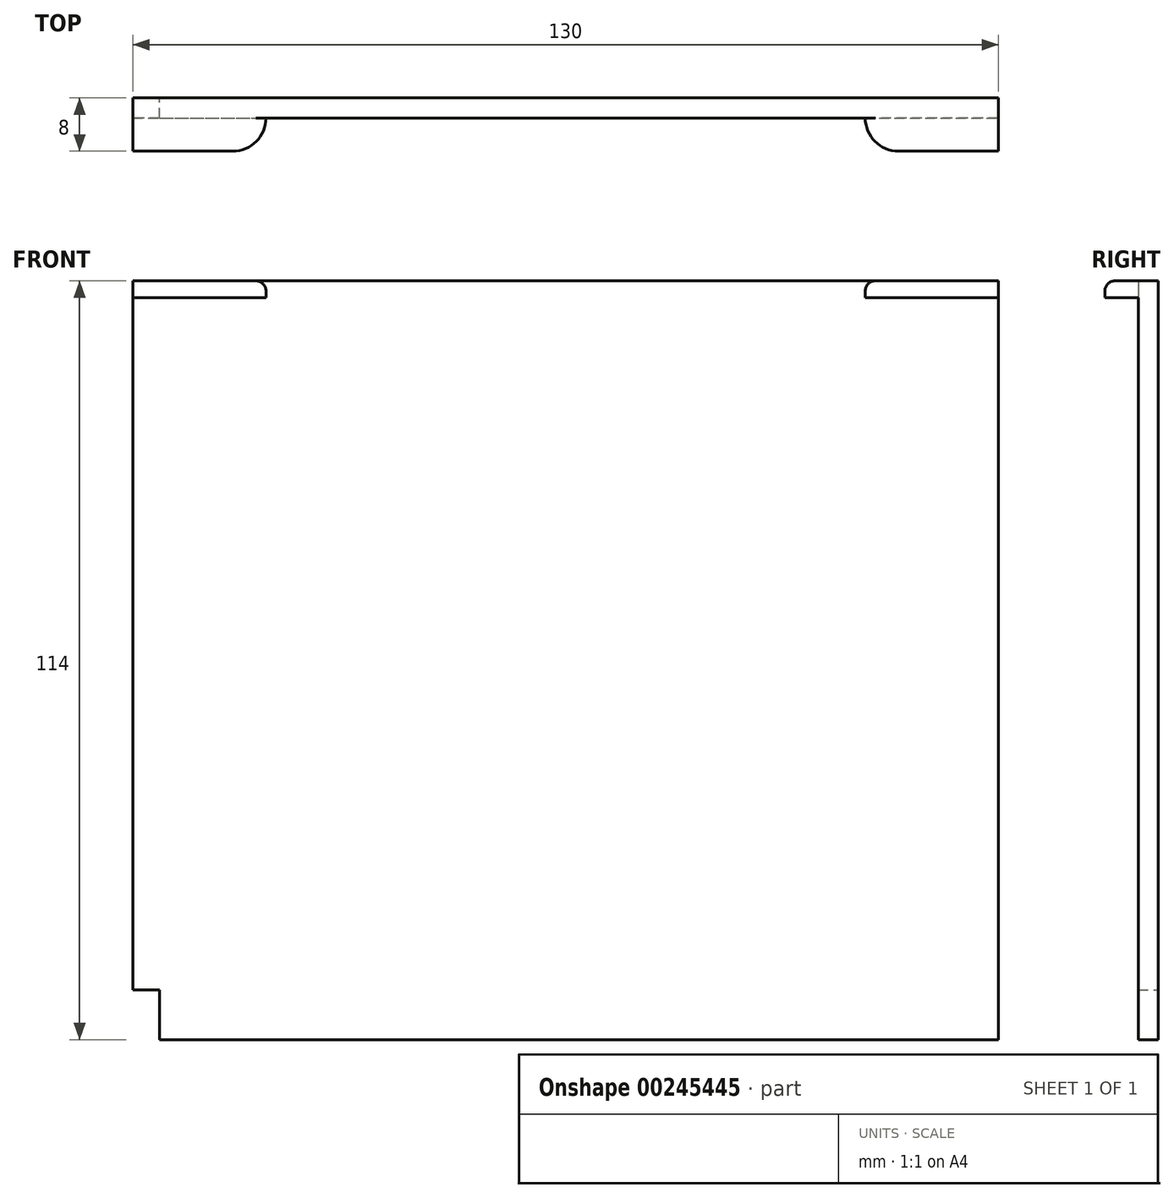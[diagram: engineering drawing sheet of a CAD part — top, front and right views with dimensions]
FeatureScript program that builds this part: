
annotation { "Feature Type Name" : "Feature", "Feature Type Description" : "" }
export const myFeature = defineFeature(function(context is Context, id is Id, definition is map)
    precondition{}
    {
        {
            var Q0;
            Q0=qCreatedBy(makeId("Front.planeOp"),FACE);
            var sketch = newSketch(context, id + "F0", { "sketchPlane" : qUnion([Q0])});
            skLineSegment(sketch, "E0.bottom", {"start": v(0, 0) * mm, "end": v(130, 0) * mm});
            skLineSegment(sketch, "E0.top", {"start": v(0, 114) * mm, "end": v(130, 114) * mm});
            skLineSegment(sketch, "E0.left", {"start": v(0, 0) * mm, "end": v(0, 114) * mm});
            skLineSegment(sketch, "E0.right", {"start": v(130, 0) * mm, "end": v(130, 114) * mm});
            skSolve(sketch);
        }
        {
            var Q0;
            Q0=qSketchRegion(id+"F0",true);
            extrude(context, id + "F1", {"entities" : qUnion([Q0]), "depth" : 3 * mm});
        }
        {
            var Q0;
            Q0=makeQuery(id+"F1.opExtrude","CAP_FACE",FACE,{"disambiguationData":[OSD([sQuery(id+"F0.wireOp",EDGE,"E0.bottom"),sQuery(id+"F0.wireOp",EDGE,"E0.top"),sQuery(id+"F0.wireOp",EDGE,"E0.left"),sQuery(id+"F0.wireOp",EDGE,"E0.right")])],"isStart":false});
            var sketch = newSketch(context, id + "F2", { "sketchPlane" : qUnion([Q0])});
            skLineSegment(sketch, "E1.bottom", {"start": v(0, 114) * mm, "end": v(20, 114) * mm});
            skLineSegment(sketch, "E1.top", {"start": v(0, 111.5) * mm, "end": v(20, 111.5) * mm});
            skLineSegment(sketch, "E1.left", {"start": v(0, 114) * mm, "end": v(0, 111.5) * mm});
            skLineSegment(sketch, "E1.right", {"start": v(20, 114) * mm, "end": v(20, 111.5) * mm});
            skLineSegment(sketch, "E2", {"start": v(65, 114) * mm, "end": v(65, 93.98) * mm});
            skPoint(sketch, "E2.endSnap0", {"position": v(65, 114) * mm});
            skLineSegment(sketch, "E3.MirrorCS", {"start": v(130, 114) * mm, "end": v(110, 114) * mm});
            skLineSegment(sketch, "E4.MirrorCS", {"start": v(130, 111.5) * mm, "end": v(110, 111.5) * mm});
            skLineSegment(sketch, "E5.MirrorCS", {"start": v(110, 114) * mm, "end": v(110, 111.5) * mm});
            skLineSegment(sketch, "E6.MirrorCS", {"start": v(130, 114) * mm, "end": v(130, 111.5) * mm});
            skSolve(sketch);
        }
        {
            var Q0;
            Q0=qSketchRegion(id+"F2",true);
            extrude(context, id + "F3", {"entities" : qUnion([Q0]), "operationType" : NewBodyOperationType.ADD, "depth" : 5 * mm});
        }
        {
            var Q0;
            Q0=makeQuery(id+"F3.opExtrude","CAP_EDGE",EDGE,{"disambiguationData":[OSD([sQuery(id+"F2.wireOp",EDGE,"E1.right")])],"isStart":false});
            var Q1;
            Q1=makeQuery(id+"F3.opExtrude","CAP_EDGE",EDGE,{"disambiguationData":[OSD([sQuery(id+"F2.wireOp",EDGE,"E5.MirrorCS")])],"isStart":false});
            fillet(context, id + "F4", {"entities" : qUnion([Q0, Q1]), "radius" : 5 * mm, "tangentPropagation" : true, "allowEdgeOverflow" : false});
        }
        {
            var Q0;
            Q0=makeQuery(id+"F3.opExtrude","CAP_EDGE",EDGE,{"disambiguationData":[OSD([sQuery(id+"F2.wireOp",EDGE,"E1.bottom")])],"isStart":false});
            var Q1;
            Q1=makeQuery(id+"F3.opExtrude","CAP_EDGE",EDGE,{"disambiguationData":[OSD([sQuery(id+"F2.wireOp",EDGE,"E3.MirrorCS")])],"isStart":false});
            fillet(context, id + "F5", {"entities" : qUnion([Q0, Q1]), "radius" : 1.5 * mm, "tangentPropagation" : true, "allowEdgeOverflow" : false});
        }
        {
            var Q0;
            Q0=makeQuery(id+"F1.opExtrude","CAP_FACE",FACE,{"disambiguationData":[OSD([sQuery(id+"F0.wireOp",EDGE,"E0.bottom"),sQuery(id+"F0.wireOp",EDGE,"E0.top"),sQuery(id+"F0.wireOp",EDGE,"E0.left"),sQuery(id+"F0.wireOp",EDGE,"E0.right")])],"isStart":true});
            var sketch = newSketch(context, id + "F6", { "sketchPlane" : qUnion([Q0])});
            skLineSegment(sketch, "E7.bottom", {"start": v(0, 0) * mm, "end": v(-4, 0) * mm});
            skLineSegment(sketch, "E7.top", {"start": v(0, 7.5) * mm, "end": v(-4, 7.5) * mm});
            skLineSegment(sketch, "E7.left", {"start": v(0, 0) * mm, "end": v(0, 7.5) * mm});
            skLineSegment(sketch, "E7.right", {"start": v(-4, 0) * mm, "end": v(-4, 7.5) * mm});
            skSolve(sketch);
        }
        {
            var Q0;
            Q0 = qSketchRegion(id + "F6", true);
            extrude(context, id + "F7", {"entities" : qUnion([Q0]), "operationType" : NewBodyOperationType.REMOVE, "oppositeDirection" : true, "depth" : 25 * mm});
        }
    });
